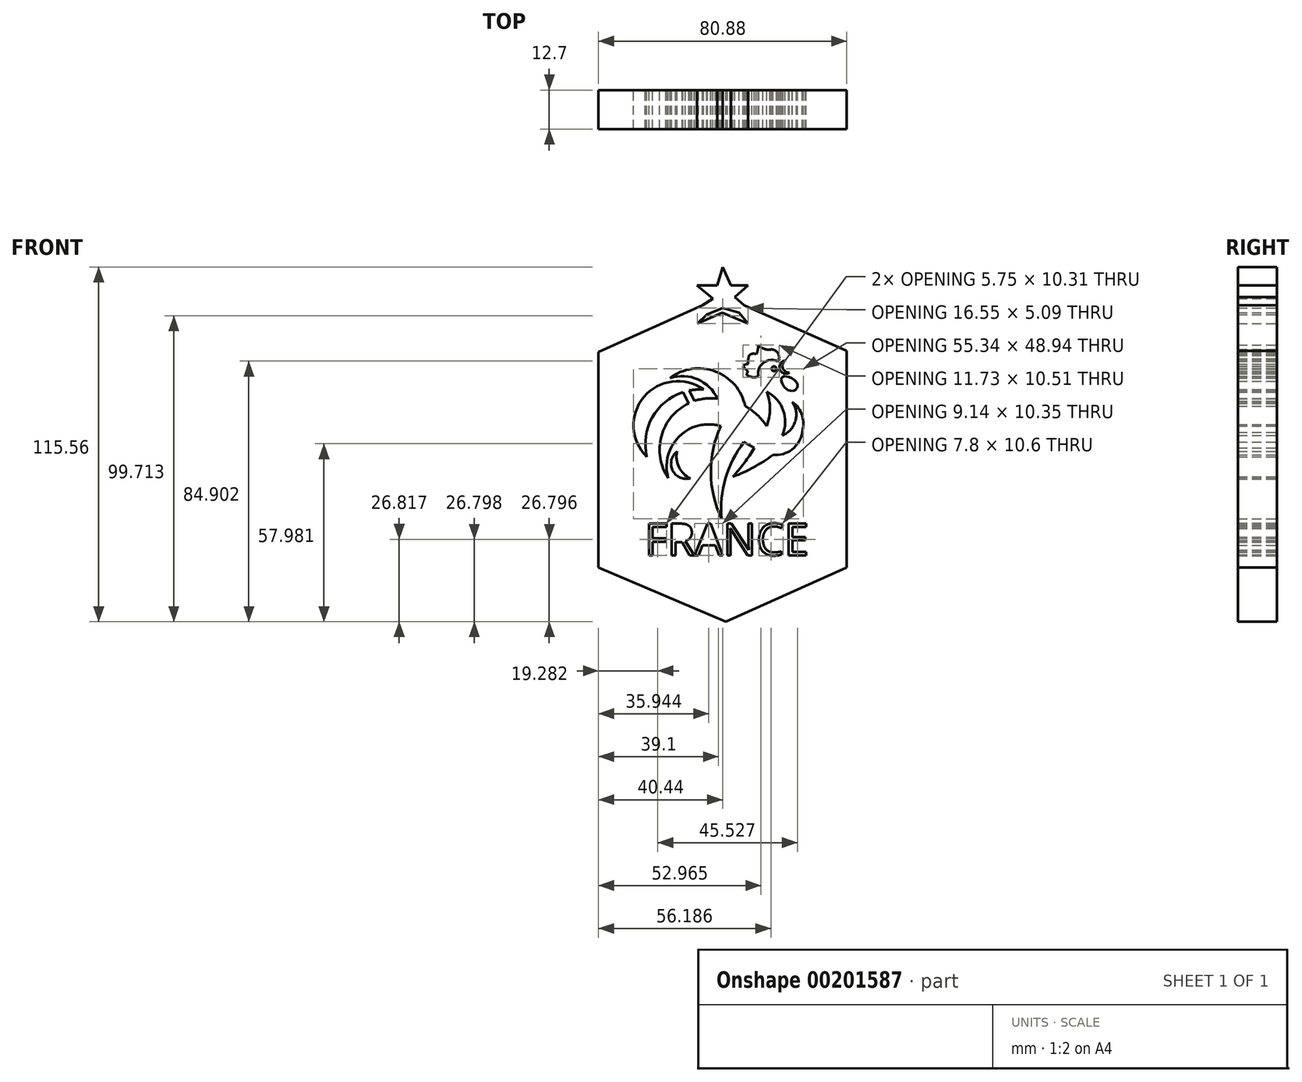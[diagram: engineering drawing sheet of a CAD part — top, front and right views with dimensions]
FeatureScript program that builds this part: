
annotation { "Feature Type Name" : "Feature", "Feature Type Description" : "" }
export const myFeature = defineFeature(function(context is Context, id is Id, definition is map)
    precondition{}
    {
        {
            var Q0;
            Q0=qCreatedBy(makeId("Front.planeOp"),FACE);
            var sketch = newSketch(context, id + "F0", { "sketchPlane" : qUnion([Q0])});
            skLineSegment(sketch, "E0", {"start": v(-45.8, 31.3) * mm, "end": v(-11.88, 46.5) * mm});
            skLineSegment(sketch, "E1", {"start": v(-11.88, 46.5) * mm, "end": v(-13.63, 40.58) * mm});
            skLineSegment(sketch, "E2", {"start": v(-13.63, 40.58) * mm, "end": v(-5.42, 44.08) * mm});
            skLineSegment(sketch, "E3", {"start": v(-5.42, 44.08) * mm, "end": v(2.93, 40.58) * mm});
            skLineSegment(sketch, "E4", {"start": v(1.72, 46.5) * mm, "end": v(35.1, 31.7) * mm});
            skLineSegment(sketch, "E5", {"start": v(35.1, 31.7) * mm, "end": v(35.1, -38.96) * mm});
            skLineSegment(sketch, "E6", {"start": v(35.1, -38.96) * mm, "end": v(-4.34, -56.6) * mm});
            skLineSegment(sketch, "E7", {"start": v(-4.34, -56.6) * mm, "end": v(-45.8, -38.96) * mm});
            skLineSegment(sketch, "E8", {"start": v(-45.8, -38.96) * mm, "end": v(-45.8, 31.3) * mm});
            skLineSegment(sketch, "E9", {"start": v(-10.53, 43.54) * mm, "end": v(-8.51, 48.65) * mm});
            skPoint(sketch, "E9.startSnap0", {"position": v(-12.75, 43.54) * mm});
            skLineSegment(sketch, "E10", {"start": v(-8.51, 48.65) * mm, "end": v(-13.76, 52.96) * mm});
            skLineSegment(sketch, "E11", {"start": v(-13.76, 52.96) * mm, "end": v(-7.17, 52.96) * mm});
            skLineSegment(sketch, "E12", {"start": v(-7.17, 52.96) * mm, "end": v(-5.4, 58.97) * mm});
            skLineSegment(sketch, "E13", {"start": v(-5.4, 58.97) * mm, "end": v(-2.7, 52.96) * mm});
            skLineSegment(sketch, "E14", {"start": v(-2.7, 52.96) * mm, "end": v(2.93, 52.96) * mm});
            skLineSegment(sketch, "E15", {"start": v(2.93, 52.96) * mm, "end": v(-1.38, 49.2) * mm});
            skLineSegment(sketch, "E16", {"start": v(-1.38, 49.2) * mm, "end": v(0, 44.08) * mm});
            skLineSegment(sketch, "E17", {"start": v(0, 44.08) * mm, "end": v(-5.4, 45.67) * mm});
            skLineSegment(sketch, "E18", {"start": v(-5.4, 45.67) * mm, "end": v(-10.53, 43.54) * mm});
            skLineSegment(sketch, "E19", {"start": v(1.72, 46.5) * mm, "end": v(-1.38, 49.2) * mm});
            skLineSegment(sketch, "E20", {"start": v(-11.88, 46.5) * mm, "end": v(-8.51, 48.65) * mm});
            skArc(sketch, "E21", {"start": v(-20.23, -1.14) * mm, "mid": v(-19.58, -6.25) * mm, "end": v(-15.92, -9.89) * mm});
            skArc(sketch, "E22", {"start": v(-20.23, -1.14) * mm, "mid": v(-21.65, -7.27) * mm, "end": v(-15.92, -9.89) * mm});
            skArc(sketch, "E23", {"start": v(-7.03, 16.08) * mm, "mid": v(-10.81, 16.14) * mm, "end": v(-14.5, 15.34) * mm});
            skArc(sketch, "E24", {"start": v(-13.76, 7.2) * mm, "mid": v(-21.93, 0.57) * mm, "end": v(-23.05, -9.89) * mm});
            skArc(sketch, "E25", {"start": v(-5.96, 7.2) * mm, "mid": v(-9.86, 7.69) * mm, "end": v(-13.76, 7.2) * mm});
            skPoint(sketch, "E26.start.orphan", {"position": v(8.98, 7.2) * mm});
            skArc(sketch, "E27", {"start": v(-7.03, 16.08) * mm, "mid": v(-13.49, 22.39) * mm, "end": v(-22.5, 22.81) * mm});
            skArc(sketch, "E28", {"start": v(1.99, 13.66) * mm, "mid": v(-7.74, 24.97) * mm, "end": v(-22.5, 22.81) * mm});
            skArc(sketch, "E29", {"start": v(8.98, 7.2) * mm, "mid": v(5.86, 10.84) * mm, "end": v(1.99, 13.66) * mm});
            skArc(sketch, "E30", {"start": v(8.98, 7.2) * mm, "mid": v(10.04, 12.79) * mm, "end": v(8.98, 18.37) * mm});
            skArc(sketch, "E31", {"start": v(14.1, 4.1) * mm, "mid": v(14.4, 12.26) * mm, "end": v(8.98, 18.37) * mm});
            skArc(sketch, "E32", {"start": v(14.1, 4.1) * mm, "mid": v(18.36, 8.77) * mm, "end": v(17.33, 15) * mm});
            skArc(sketch, "E33", {"start": v(20.56, 5.18) * mm, "mid": v(20.54, 10.62) * mm, "end": v(17.33, 15) * mm});
            skArc(sketch, "E34", {"start": v(11, -2.22) * mm, "mid": v(17.27, -0.45) * mm, "end": v(20.56, 5.18) * mm});
            skArc(sketch, "E35", {"start": v(-2.05, -9.35) * mm, "mid": v(4.74, -6.27) * mm, "end": v(11, -2.22) * mm});
            skArc(sketch, "E36", {"start": v(-2.05, -9.35) * mm, "mid": v(1.71, -4.87) * mm, "end": v(4.95, 0) * mm});
            skLineSegment(sketch, "E37", {"start": v(4.95, 0) * mm, "end": v(1.58, 1.95) * mm});
            skArc(sketch, "E38", {"start": v(1.58, 1.95) * mm, "mid": v(-4.4, -9.88) * mm, "end": v(-5.69, -23.08) * mm});
            skArc(sketch, "E39", {"start": v(-5.96, 7.2) * mm, "mid": v(-9.2, -7.97) * mm, "end": v(-5.69, -23.08) * mm});
            skArc(sketch, "E40", {"start": v(-11.6, 19.04) * mm, "mid": v(-31, 16.63) * mm, "end": v(-30.05, -2.9) * mm});
            skArc(sketch, "E41", {"start": v(-11.6, 19.04) * mm, "mid": v(-13.93, 19.04) * mm, "end": v(-16.24, 18.74) * mm});
            skLineSegment(sketch, "E42", {"start": v(-18.28, 18.2) * mm, "end": v(-16.43, 14.56) * mm});
            skLineSegment(sketch, "E43", {"start": v(-14.5, 15.34) * mm, "end": v(-16.43, 19.1) * mm});
            skArc(sketch, "E44.trimOffspring", {"start": v(-18.28, 18.2) * mm, "mid": v(-28.3, 9.95) * mm, "end": v(-30.05, -2.9) * mm});
            skArc(sketch, "E45.trimOffspring", {"start": v(-16.43, 14.56) * mm, "mid": v(-25.33, 3.85) * mm, "end": v(-23.05, -9.89) * mm});
            skFitSpline(sketch, "E46", {"points": [v(14.23, 23.22) * mm, v(18.8, 21.33) * mm, v(18, 18.77) * mm, v(14.64, 19.99) * mm, v(14.23, 23.22) * mm]});
            skArc(sketch, "E47", {"start": v(15.04, 28.46) * mm, "mid": v(14.26, 26.01) * mm, "end": v(16.39, 24.56) * mm});
            skArc(sketch, "E48", {"start": v(15.04, 28.46) * mm, "mid": v(13.27, 25.67) * mm, "end": v(16.39, 24.56) * mm});
            skCircle(sketch, "E49", {"center": v(11.39, 25.83) * mm, "radius": 0.78 * mm});
            skArc(sketch, "E50", {"start": v(2.29, 24.12) * mm, "mid": v(4.18, 23.1) * mm, "end": v(6.3, 23.44) * mm});
            skArc(sketch, "E51", {"start": v(2.29, 24.12) * mm, "mid": v(2.74, 25.06) * mm, "end": v(1.88, 25.66) * mm});
            skLineSegment(sketch, "E52", {"start": v(1.88, 25.66) * mm, "end": v(1.31, 26.67) * mm});
            skArc(sketch, "E53", {"start": v(3, 27.38) * mm, "mid": v(2.08, 27.21) * mm, "end": v(1.31, 26.67) * mm});
            skArc(sketch, "E54", {"start": v(3.26, 30.2) * mm, "mid": v(2.99, 28.8) * mm, "end": v(3, 27.38) * mm});
            skArc(sketch, "E55", {"start": v(5.65, 30.54) * mm, "mid": v(4.4, 30.73) * mm, "end": v(3.26, 30.2) * mm});
            skArc(sketch, "E56", {"start": v(5.65, 30.54) * mm, "mid": v(6.1, 32.03) * mm, "end": v(6.22, 33.57) * mm});
            skArc(sketch, "E57", {"start": v(6.22, 33.57) * mm, "mid": v(8.23, 32.3) * mm, "end": v(10.6, 32.12) * mm});
            skArc(sketch, "E58", {"start": v(12.99, 29.1) * mm, "mid": v(12.49, 31.16) * mm, "end": v(10.6, 32.12) * mm});
            skArc(sketch, "E59", {"start": v(12.65, 28.19) * mm, "mid": v(13, 28.58) * mm, "end": v(12.99, 29.1) * mm});
            skArc(sketch, "E60", {"start": v(12.65, 28.19) * mm, "mid": v(7.98, 27.82) * mm, "end": v(6.3, 23.44) * mm});
            skText(sketch, "E61", { "text": "FRANCE", "fontName": "OpenSans-Regular.ttf"});
            skPoint(sketch, "E62.end.orphan", {"position": v(1.72, 43.36) * mm});
            skLineSegment(sketch, "E63", {"start": v(1.72, 46.5) * mm, "end": v(2.93, 40.58) * mm});
            skLineSegment(sketch, "E64", {"start": v(0, 44.08) * mm, "end": v(2.93, 40.58) * mm});
            skLineSegment(sketch, "E65", {"start": v(-10.53, 43.54) * mm, "end": v(-13.63, 40.58) * mm});
            const initialGuessF0  = {"E61": [-0.0308, -0.03495, 1, 0, 0.0104]};
            skSetInitialGuess(sketch, initialGuessF0);
            skSolve(sketch);
        }
        {
            var Q0;
            {var subQ1=sQuery(id+"F0.wireOp",EDGE,"E0");Q0=makeQuery(id+"F0.imprint","IMPRINT",FACE,{"disambiguationData":[TD([[makeQuery(id+"F0.imprint","IMPRINT",EDGE,{"derivedFrom":subQ1}),-1.0]])]});}
            var Q1;
            Q1=makeQuery(id+"F0.imprint","IMPRINT",FACE,{"disambiguationData":[TD([[makeQuery(id+"F0.imprint","IMPRINT",EDGE,{"derivedFrom":sQuery(id+"F0.wireOp",EDGE,"E9")}),-1.0]])]});
            var Q2;
            Q2=makeQuery(id+"F0.imprint","IMPRINT",FACE,{"disambiguationData":[TD([[makeQuery(id+"F0.imprint","IMPRINT",EDGE,{"derivedFrom":sQuery(id+"F0.wireOp",EDGE,"E9")}),1.0]])]});
            var Q3;
            Q3=makeQuery(id+"F0.imprint","IMPRINT",FACE,{"disambiguationData":[TD([[makeQuery(id+"F0.imprint","IMPRINT",EDGE,{"derivedFrom":sQuery(id+"F0.wireOp",EDGE,"E16")}),1.0]])]});
            extrude(context, id + "F1", {"entities" : qUnion([Q0, Q1, Q2, Q3]), "depth" : 12.7 * mm});
        }
    });
